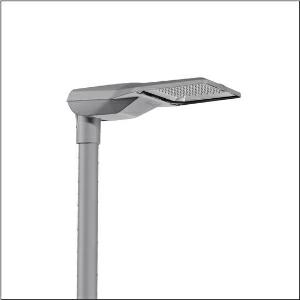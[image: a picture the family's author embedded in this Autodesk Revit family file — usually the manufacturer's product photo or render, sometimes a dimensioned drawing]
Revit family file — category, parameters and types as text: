
# Revit family: streetlight_sl_21_iq_midi___pc-l_5xe3f31g08mb_a45c
name_source: partatom
category: Lighting Fixtures
units: mm (PartAtom-declared; Revit-internal decimal feet)

## family parameters
Cut with Voids When Loaded = No
Host = Face
Light Source = No
Part Type = Normal
Room Calculation Point = No
Round Connector Dimension = Use Diameter
Shared = No

## types (1)
- --- (1 x LED, 18560 lm, 146.7 W, 3000K)
    Apparent Load = 147 VA
    CIE Flux Codes = 38 78 98 100 100
    Color Rendering = 70
    Color Temperature = 3000K
    Default Elevation = 1800 mm
    Description = Streetlight SL 21 iQ midi, mast luminaire, primary light control with lens, of PMMA, primary optical cover: cover, of toughened safety glass, transparent, light distribution: PC-L, light emission: direct distribution, primary light characteristic: asymmetric, left, installation type: post-top, side-entry, LED, High Power LED, rated luminous flux: 18.560lm, luminous efficacy: 127lm/W, light colour: 730, colour temperature: 3000K, control: Street-Remote, Auto-Match, Temp-Guard, Lumen-Switch, Night-Set, Smart-Wire, Light-Fading, Desk-Remote (wireless, voltage-free reading and setting of iQ features in the workshop via application-optimized NFC function/RFID function), optimised constant luminous flux control (CLO 2.0), presetting dimming linear, mains connection: 230..240V, AC, 50/60Hz, start of lifetime: 147W, end of service life: 161W, reduction: 62W, luminaire housing, of diecast aluminium, powder-coated, Siteco® metallic grey (DB 702S), corrosivity category C5 mid according to DIN EN ISO 12944, please order mast flange separately, inclination adjustable: 0°, 5°, 10°, 15°, sealing non-destructively replaceable, multi-level sealing system, length: 644mm, width: 335mm, height: 110mm, mast flange for spigot size: 42mm (side-entry): 5XC10008XM4, 60/48mm (side-entry/post-top): 5XC10108XM2, 76/60mm (side-entry/post-top): 5XC10108XM1, protection rating (complete): IP66, insulation class (complete): insulation class II (safety insulation), certification: CE, ENEC, ENEC+, VDE, impact resistance: IK09, permissible operating ambient temperature for outdoor applications: -40..+50°C, standard-compliant lighting for roads and squares, packaging unit: 1 piece

Light Distribution: PC-L
    Height = 111 mm
    Lamp = 1 x LED
    Lamp Light Flux = 18560 lm
    Lamp Power = 146.7 W
    Lamp count = 1
    Length = 644 mm
    Luminous efficacy = 127 lm/W
    Manufacturer = Siteco
    ModVariant = No
    Model = 5XE3F31G08MB
    Number of Poles = 1
    OnlyDefault = Yes
    Power Factor = 1
    Product Name = Streetlight SL 21 iQ midi | PC-L
    Product group = mast luminaire | pylon top
    ProductGroupID = 6100
    Protection Class = Protection class II
    Protection Degree = IP 66
    RLX_Detail_Level = 1
    RLX_Emergency_Light_Flux = 0 lm
    RLX_Emergency_Type = 0
    RLX_Emergency_Type_DB = No
    RlxData = <blob elided: 93133 chars, md5=a0fb3e69>
    Socket = socket
    Standby Power = 0 W
    System Light Flux = 18560 lm
    System Power = 147 W
    Type Comments = factory setting: luminous flux: 100 % | dim-lin: 254 | 753 mA
    Type Image = l_1004298.jpg
    URL = http://relux.com
    VarID = @adj_005485
    Voltage = 0 V
    Weight = 0.00 kg
    Width = 336 mm

## geometry (parser evidence)
native form markers: Blend x4, Sweep x9
no freeform markers — native parametric forms only
